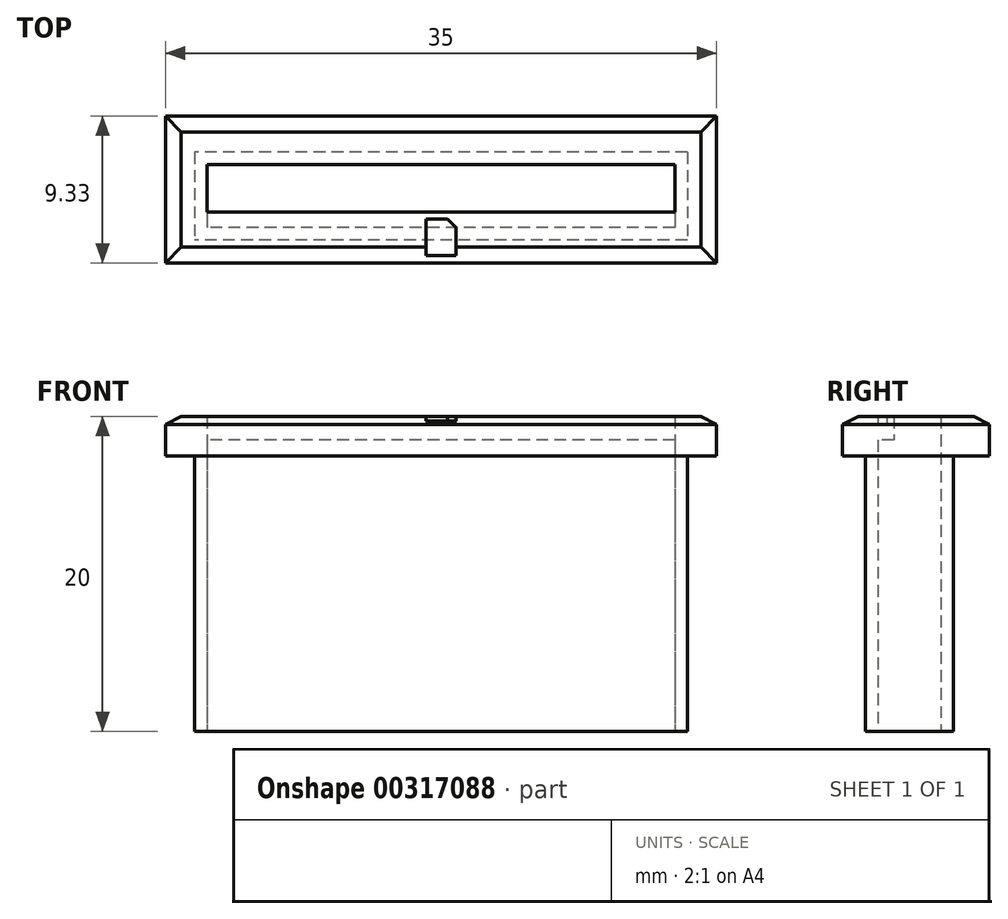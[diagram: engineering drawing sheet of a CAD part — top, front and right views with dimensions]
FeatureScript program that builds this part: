
annotation { "Feature Type Name" : "Feature", "Feature Type Description" : "" }
export const myFeature = defineFeature(function(context is Context, id is Id, definition is map)
    precondition{}
    {
        {
            var Q0;
            Q0=qCreatedBy(makeId("Top.planeOp"),FACE);
            var sketch = newSketch(context, id + "F0", { "sketchPlane" : qUnion([Q0])});
            skLineSegment(sketch, "E0.bottom", {"start": v(14.85, 2) * mm, "end": v(-14.85, 2) * mm});
            skLineSegment(sketch, "E0.top", {"start": v(14.85, -2) * mm, "end": v(-14.85, -2) * mm});
            skLineSegment(sketch, "E0.left", {"start": v(14.85, 2) * mm, "end": v(14.85, -2) * mm});
            skLineSegment(sketch, "E0.right", {"start": v(-14.85, 2) * mm, "end": v(-14.85, -2) * mm});
            skPoint(sketch, "E0.middle", {"position": v(0, 0) * mm});
            skLineSegment(sketch, "E1", {"start": v(-14.85, -1) * mm, "end": v(14.85, -1) * mm});
            skLineSegment(sketch, "E2.top", {"start": v(17.5, -4.25) * mm, "end": v(-17.5, -4.25) * mm});
            skLineSegment(sketch, "E3.bottom", {"start": v(15.65, 2.8) * mm, "end": v(-15.65, 2.8) * mm});
            skLineSegment(sketch, "E3.top", {"start": v(15.65, -2.8) * mm, "end": v(-15.65, -2.8) * mm});
            skLineSegment(sketch, "E3.left", {"start": v(15.65, 2.8) * mm, "end": v(15.65, -2.8) * mm});
            skLineSegment(sketch, "E3.right", {"start": v(-15.65, 2.8) * mm, "end": v(-15.65, -2.8) * mm});
            skLineSegment(sketch, "E4.bottom", {"start": v(0.41, -1.45) * mm, "end": v(-0.96, -1.45) * mm});
            skLineSegment(sketch, "E4.top", {"start": v(0.96, -3.79) * mm, "end": v(-0.96, -3.79) * mm});
            skLineSegment(sketch, "E4.left", {"start": v(0.96, -2) * mm, "end": v(0.96, -3.79) * mm});
            skLineSegment(sketch, "E4.right", {"start": v(-0.96, -1.45) * mm, "end": v(-0.96, -3.79) * mm});
            skPoint(sketch, "E4.middle", {"position": v(0, -2.62) * mm});
            skLineSegment(sketch, "E5", {"start": v(0.41, -1.45) * mm, "end": v(0.96, -2) * mm});
            skPoint(sketch, "E6.orphan", {"position": v(0.96, -1.45) * mm});
            skLineSegment(sketch, "E7", {"start": v(-17.5, 5.08) * mm, "end": v(17.5, 5.08) * mm});
            skPoint(sketch, "E2.left.start.orphan", {"position": v(17.5, 4.25) * mm});
            skLineSegment(sketch, "E8", {"start": v(17.5, 5.08) * mm, "end": v(17.5, -4.25) * mm});
            skLineSegment(sketch, "E9", {"start": v(-17.5, 5.08) * mm, "end": v(-17.5, -4.25) * mm});
            skSolve(sketch);
        }
        {
            var Q0;
            {var subQ4=sQuery(id+"F0.wireOp",EDGE,"E0.bottom");Q0=makeQuery(id+"F0.imprint","IMPRINT",FACE,{"disambiguationData":[TD([[makeQuery(id+"F0.imprint","IMPRINT",EDGE,{"derivedFrom":subQ4}),-1.0]])]});}
            extrude(context, id + "F1", {"entities" : qUnion([Q0]), "depth" : 20 * mm});
        }
        {
            var Q0;
            {var subQ0=sQuery(id+"F0.wireOp",EDGE,"E0.top");Q0=makeQuery(id+"F0.imprint","IMPRINT",FACE,{"disambiguationData":[TD([[makeQuery(id+"F0.imprint","IMPRINT",EDGE,{"derivedFrom":subQ0}),-1.0]])]});}
            extrude(context, id + "F2", {"entities" : qUnion([Q0]), "operationType" : NewBodyOperationType.ADD, "depth" : 20 * mm, "hasSecondDirection" : true, "secondDirectionOppositeDirection" : false, "secondDirectionDepth" : 18.5 * mm});
        }
        {
            var Q0;
            {var subQ0=sQuery(id+"F0.wireOp",EDGE,"E4.left");var subQ5=sQuery(id+"F0.wireOp",EDGE,"E3.top");var subQ6=makeQuery(id+"F0.imprint","INTERSECT",VERTEX,{"derivedFrom":[subQ5,subQ0]});Q0=makeQuery(id+"F0.imprint","IMPRINT",FACE,{"disambiguationData":[TD([[makeQuery(id+"F0.imprint","IMPRINT",EDGE,{"disambiguationData":[TD([[subQ6,-1.0]])],"derivedFrom":subQ5}),-1.0]])]});}
            var Q1;
            {var subQ4=sQuery(id+"F0.wireOp",EDGE,"E4.bottom");Q1=makeQuery(id+"F0.imprint","IMPRINT",FACE,{"disambiguationData":[TD([[makeQuery(id+"F0.imprint","IMPRINT",EDGE,{"derivedFrom":subQ4}),1.0]])]});}
            extrude(context, id + "F3", {"entities" : qUnion([Q0, Q1]), "operationType" : NewBodyOperationType.ADD, "depth" : 19.5 * mm, "hasSecondDirection" : true, "secondDirectionOppositeDirection" : false, "secondDirectionDepth" : 17.5 * mm});
        }
        {
            var Q0;
            {var subQ5=sQuery(id+"F0.wireOp",EDGE,"E4.top");Q0=makeQuery(id+"F0.imprint","IMPRINT",FACE,{"disambiguationData":[TD([[makeQuery(id+"F0.imprint","IMPRINT",EDGE,{"derivedFrom":subQ5}),-1.0]])]});}
            extrude(context, id + "F4", {"entities" : qUnion([Q0]), "operationType" : NewBodyOperationType.ADD, "depth" : 19.5 * mm, "hasSecondDirection" : true, "secondDirectionOppositeDirection" : false, "secondDirectionDepth" : 17.5 * mm});
        }
        {
            var Q0;
            {var subQ0=sQuery(id+"F0.wireOp",EDGE,"E4.left");var subQ5=sQuery(id+"F0.wireOp",EDGE,"E3.top");var subQ6=makeQuery(id+"F0.imprint","INTERSECT",VERTEX,{"derivedFrom":[subQ5,subQ0]});Q0=makeQuery(id+"F0.imprint","IMPRINT",FACE,{"disambiguationData":[TD([[makeQuery(id+"F0.imprint","IMPRINT",EDGE,{"disambiguationData":[TD([[subQ6,-1.0]])],"derivedFrom":subQ5}),-1.0]])]});}
            extrude(context, id + "F5", {"entities" : qUnion([Q0]), "operationType" : NewBodyOperationType.ADD, "depth" : 17.5 * mm});
        }
        {
            var Q0;
            {var subQ4=sQuery(id+"F0.wireOp",EDGE,"E4.bottom");Q0=makeQuery(id+"F0.imprint","IMPRINT",FACE,{"disambiguationData":[TD([[makeQuery(id+"F0.imprint","IMPRINT",EDGE,{"derivedFrom":subQ4}),1.0]])]});}
            extrude(context, id + "F6", {"entities" : qUnion([Q0]), "operationType" : NewBodyOperationType.REMOVE, "depth" : 18.5 * mm});
        }
        {
            var Q0;
            Q0=makeQuery(id+"F0.imprint","IMPRINT",FACE,{"disambiguationData":[TD([[makeQuery(id+"F0.imprint","IMPRINT",EDGE,{"derivedFrom":sQuery(id+"F0.wireOp",EDGE,"E2.top")}),-1.0]])]});
            extrude(context, id + "F7", {"entities" : qUnion([Q0]), "operationType" : NewBodyOperationType.ADD, "depth" : 20 * mm, "hasSecondDirection" : true, "secondDirectionOppositeDirection" : false, "secondDirectionDepth" : 17.5 * mm});
        }
        {
            var Q0;
            Q0=makeQuery(id+"F7.opExtrude","CAP_EDGE",EDGE,{"disambiguationData":[OSD([sQuery(id+"F0.wireOp",EDGE,"E7")])],"isStart":false});
            var Q1;
            Q1=makeQuery(id+"F7.opExtrude","CAP_EDGE",EDGE,{"disambiguationData":[OSD([sQuery(id+"F0.wireOp",EDGE,"E9")])],"isStart":false});
            var Q2;
            Q2=makeQuery(id+"F7.opExtrude","CAP_EDGE",EDGE,{"disambiguationData":[OSD([sQuery(id+"F0.wireOp",EDGE,"E8")])],"isStart":false});
            var Q3;
            Q3=makeQuery(id+"F7.opExtrude","CAP_EDGE",EDGE,{"disambiguationData":[OSD([sQuery(id+"F0.wireOp",EDGE,"E2.top")])],"isStart":false});
            chamfer(context, id + "F8", {"entities" : qUnion([Q0, Q1, Q2, Q3]), "chamferType" : ChamferType.TWO_OFFSETS, "width1" : 0.5 * mm, "oppositeDirection" : false, "width2" : 1 * mm, "tangentPropagation" : true});
        }
    });
